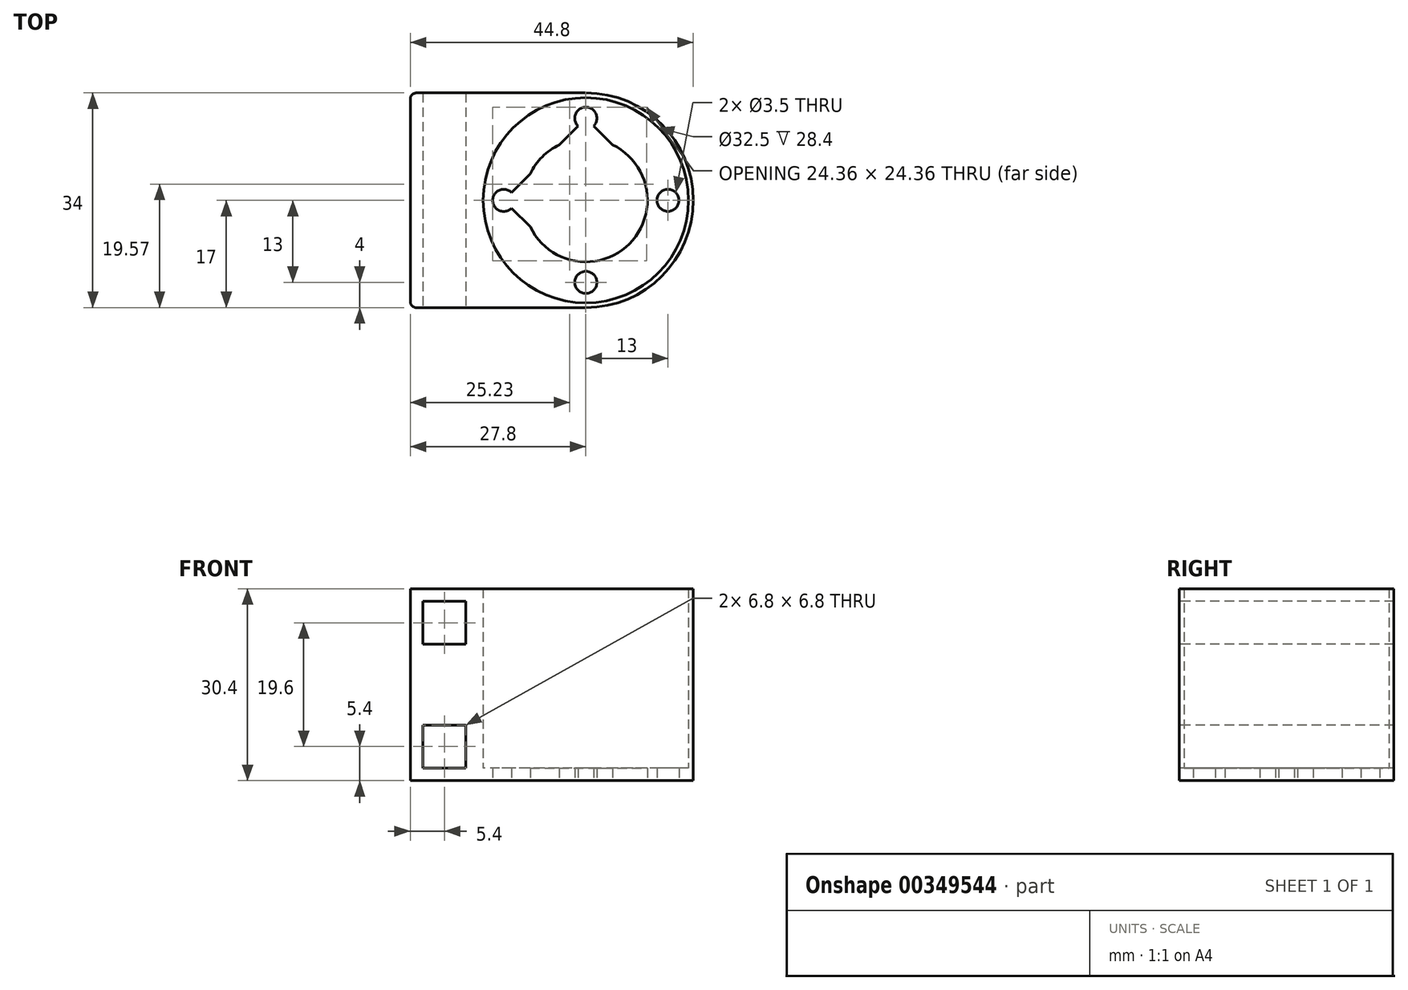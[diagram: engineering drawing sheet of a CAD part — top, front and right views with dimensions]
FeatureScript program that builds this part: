
annotation { "Feature Type Name" : "Feature", "Feature Type Description" : "" }
export const myFeature = defineFeature(function(context is Context, id is Id, definition is map)
    precondition{}
    {
        {
            var Q0;
            Q0=qCreatedBy(makeId("Top.planeOp"),FACE);
            var sketch = newSketch(context, id + "F0", { "sketchPlane" : qUnion([Q0])});
            skCircle(sketch, "E0", {"center": v(0, 0) * mm, "radius": 16.25 * mm});
            skCircle(sketch, "E1", {"center": v(0, 0) * mm, "radius": 17 * mm});
            skLineSegment(sketch, "E2", {"start": v(0, 0) * mm, "end": v(0, 17) * mm});
            skLineSegment(sketch, "E3.bottom", {"start": v(0, 17) * mm, "end": v(-27.8, 17) * mm});
            skLineSegment(sketch, "E3.top", {"start": v(0, -17) * mm, "end": v(-27.8, -17) * mm});
            skLineSegment(sketch, "E3.left", {"start": v(0, 17) * mm, "end": v(0, -17) * mm});
            skLineSegment(sketch, "E3.right", {"start": v(-27.8, 17) * mm, "end": v(-27.8, -17) * mm});
            skCircle(sketch, "E4", {"center": v(0, 0) * mm, "radius": 9.75 * mm});
            skCircle(sketch, "E5.cCircle", {"center": v(0, 0) * mm, "radius": 13 * mm, "construction": true});
            skLineSegment(sketch, "E5.0", {"start": v(0, -13) * mm, "end": v(-13, 0) * mm});
            skLineSegment(sketch, "E5.1", {"start": v(-13, 0) * mm, "end": v(0, 13) * mm});
            skLineSegment(sketch, "E5.2", {"start": v(0, 13) * mm, "end": v(13, 0) * mm});
            skLineSegment(sketch, "E5.3", {"start": v(13, 0) * mm, "end": v(0, -13) * mm});
            skCircle(sketch, "E6", {"center": v(0, 13) * mm, "radius": 1.75 * mm});
            skCircle(sketch, "E7", {"center": v(13, 0) * mm, "radius": 1.75 * mm});
            skCircle(sketch, "E8", {"center": v(0, -13) * mm, "radius": 1.75 * mm});
            skCircle(sketch, "E9", {"center": v(-13, 0) * mm, "radius": 1.75 * mm});
            skSolve(sketch);
        }
        {
            var Q0;
            {var subQ1=sQuery(id+"F0.wireOp",EDGE,"E3.bottom");Q0=makeQuery(id+"F0.imprint","IMPRINT",FACE,{"disambiguationData":[TD([[makeQuery(id+"F0.imprint","IMPRINT",EDGE,{"derivedFrom":subQ1}),1.0]])]});}
            var Q1;
            {var subQ0=sQuery(id+"F0.wireOp",EDGE,"E3.left");var subQ1=sQuery(id+"F0.wireOp",EDGE,"E0");var subQ2=makeQuery(id+"F0.imprint","INTERSECT",VERTEX,{"disambiguationData":[OD(0.0)],"derivedFrom":[subQ1,subQ0]});Q1=makeQuery(id+"F0.imprint","IMPRINT",FACE,{"disambiguationData":[TD([[makeQuery(id+"F0.imprint","IMPRINT",EDGE,{"disambiguationData":[TD([[subQ2,-1.0]])],"derivedFrom":subQ1}),-1.0]])]});}
            var Q2;
            {var subQ0=sQuery(id+"F0.wireOp",EDGE,"E3.left");var subQ1=sQuery(id+"F0.wireOp",EDGE,"E0");var subQ2=makeQuery(id+"F0.imprint","INTERSECT",VERTEX,{"disambiguationData":[OD(0.0)],"derivedFrom":[subQ1,subQ0]});Q2=makeQuery(id+"F0.imprint","IMPRINT",FACE,{"disambiguationData":[TD([[makeQuery(id+"F0.imprint","IMPRINT",EDGE,{"disambiguationData":[TD([[subQ2,1.0]])],"derivedFrom":subQ1}),-1.0]])]});}
            extrude(context, id + "F1", {"entities" : qUnion([Q0, Q1, Q2]), "depth" : 30.4 * mm});
        }
        {
            var Q0;
            {var subQ5=sQuery(id+"F0.wireOp",EDGE,"E3.left");var subQ6=sQuery(id+"F0.wireOp",EDGE,"E0");var subQ7=makeQuery(id+"F0.imprint","INTERSECT",VERTEX,{"disambiguationData":[OD(0.0)],"derivedFrom":[subQ6,subQ5]});Q0=makeQuery(id+"F0.imprint","IMPRINT",FACE,{"disambiguationData":[TD([[makeQuery(id+"F0.imprint","IMPRINT",EDGE,{"disambiguationData":[TD([[subQ7,1.0]])],"derivedFrom":subQ6}),1.0]])]});}
            var Q1;
            {var subQ12=sQuery(id+"F0.wireOp",EDGE,"E3.left");var subQ13=sQuery(id+"F0.wireOp",EDGE,"E0");var subQ14=makeQuery(id+"F0.imprint","INTERSECT",VERTEX,{"disambiguationData":[OD(0.0)],"derivedFrom":[subQ13,subQ12]});Q1=makeQuery(id+"F0.imprint","IMPRINT",FACE,{"disambiguationData":[TD([[makeQuery(id+"F0.imprint","IMPRINT",EDGE,{"disambiguationData":[TD([[subQ14,-1.0]])],"derivedFrom":subQ13}),1.0]])]});}
            var Q2;
            {var subQ0=sQuery(id+"F0.wireOp",EDGE,"E6");var subQ1=sQuery(id+"F0.wireOp",EDGE,"E3.left");var subQ2=makeQuery(id+"F0.imprint","INTERSECT",VERTEX,{"disambiguationData":[OD(1.0)],"derivedFrom":[subQ1,subQ0]});Q2=makeQuery(id+"F0.imprint","IMPRINT",FACE,{"disambiguationData":[TD([[makeQuery(id+"F0.imprint","IMPRINT",EDGE,{"disambiguationData":[TD([[subQ2,-1.0]])],"derivedFrom":subQ1}),-1.0]])]});}
            var Q3;
            {var subQ0=sQuery(id+"F0.wireOp",EDGE,"E6");var subQ1=sQuery(id+"F0.wireOp",EDGE,"E3.left");var subQ2=makeQuery(id+"F0.imprint","INTERSECT",VERTEX,{"disambiguationData":[OD(1.0)],"derivedFrom":[subQ1,subQ0]});Q3=makeQuery(id+"F0.imprint","IMPRINT",FACE,{"disambiguationData":[TD([[makeQuery(id+"F0.imprint","IMPRINT",EDGE,{"disambiguationData":[TD([[subQ2,-1.0]])],"derivedFrom":subQ1}),1.0]])]});}
            var Q4;
            {var subQ0=sQuery(id+"F0.wireOp",EDGE,"E5.1");var subQ1=sQuery(id+"F0.wireOp",EDGE,"E4");var subQ2=makeQuery(id+"F0.imprint","INTERSECT",VERTEX,{"disambiguationData":[OD(1.0)],"derivedFrom":[subQ1,subQ0]});Q4=makeQuery(id+"F0.imprint","IMPRINT",FACE,{"disambiguationData":[TD([[makeQuery(id+"F0.imprint","IMPRINT",EDGE,{"disambiguationData":[TD([[subQ2,-1.0]])],"derivedFrom":subQ1}),-1.0]])]});}
            var Q5;
            {var subQ0=sQuery(id+"F0.wireOp",EDGE,"E5.2");var subQ1=sQuery(id+"F0.wireOp",EDGE,"E4");var subQ2=makeQuery(id+"F0.imprint","INTERSECT",VERTEX,{"disambiguationData":[OD(1.0)],"derivedFrom":[subQ1,subQ0]});Q5=makeQuery(id+"F0.imprint","IMPRINT",FACE,{"disambiguationData":[TD([[makeQuery(id+"F0.imprint","IMPRINT",EDGE,{"disambiguationData":[TD([[subQ2,1.0]])],"derivedFrom":subQ1}),-1.0]])]});}
            var Q6;
            {var subQ0=sQuery(id+"F0.wireOp",EDGE,"E4");var subQ1=sQuery(id+"F0.wireOp",EDGE,"E3.left");var subQ2=makeQuery(id+"F0.imprint","INTERSECT",VERTEX,{"disambiguationData":[OD(1.0)],"derivedFrom":[subQ1,subQ0]});Q6=makeQuery(id+"F0.imprint","IMPRINT",FACE,{"disambiguationData":[TD([[makeQuery(id+"F0.imprint","IMPRINT",EDGE,{"disambiguationData":[TD([[subQ2,-1.0]])],"derivedFrom":subQ1}),1.0]])]});}
            var Q7;
            {var subQ0=sQuery(id+"F0.wireOp",EDGE,"E4");var subQ1=sQuery(id+"F0.wireOp",EDGE,"E3.left");var subQ2=makeQuery(id+"F0.imprint","INTERSECT",VERTEX,{"disambiguationData":[OD(1.0)],"derivedFrom":[subQ1,subQ0]});Q7=makeQuery(id+"F0.imprint","IMPRINT",FACE,{"disambiguationData":[TD([[makeQuery(id+"F0.imprint","IMPRINT",EDGE,{"disambiguationData":[TD([[subQ2,-1.0]])],"derivedFrom":subQ1}),-1.0]])]});}
            extrude(context, id + "F2", {"entities" : qUnion([Q0, Q1, Q2, Q3, Q4, Q5, Q6, Q7]), "operationType" : NewBodyOperationType.ADD, "depth" : 2 * mm});
        }
        {
            var Q0;
            Q0=makeQuery(id+"F1.opExtrude","SWEPT_FACE",FACE,{"disambiguationData":[OSD([sQuery(id+"F0.wireOp",EDGE,"E3.top")])]});
            var sketch = newSketch(context, id + "F3", { "sketchPlane" : qUnion([Q0])});
            skLineSegment(sketch, "E10.bottom", {"start": v(-27.8, 30.4) * mm, "end": v(-25.8, 30.4) * mm});
            skLineSegment(sketch, "E10.top", {"start": v(-27.8, 28.4) * mm, "end": v(-25.8, 28.4) * mm});
            skLineSegment(sketch, "E10.left", {"start": v(-27.8, 30.4) * mm, "end": v(-27.8, 28.4) * mm});
            skLineSegment(sketch, "E10.right", {"start": v(-25.8, 30.4) * mm, "end": v(-25.8, 28.4) * mm});
            skLineSegment(sketch, "E11.bottom", {"start": v(-25.8, 28.4) * mm, "end": v(-19, 28.4) * mm});
            skLineSegment(sketch, "E11.top", {"start": v(-25.8, 21.6) * mm, "end": v(-19, 21.6) * mm});
            skLineSegment(sketch, "E11.left", {"start": v(-25.8, 28.4) * mm, "end": v(-25.8, 21.6) * mm});
            skLineSegment(sketch, "E11.right", {"start": v(-19, 28.4) * mm, "end": v(-19, 21.6) * mm});
            skPoint(sketch, "E12", {"position": v(-27.8, 15.2) * mm});
            skLineSegment(sketch, "E13", {"start": v(-27.8, 15.2) * mm, "end": v(0, 15.2) * mm});
            skLineSegment(sketch, "E14.MirrorCS", {"start": v(-25.8, 8.8) * mm, "end": v(-19, 8.8) * mm});
            skLineSegment(sketch, "E15.MirrorCS", {"start": v(-19, 2) * mm, "end": v(-19, 8.8) * mm});
            skLineSegment(sketch, "E16.MirrorCS", {"start": v(-25.8, 2) * mm, "end": v(-19, 2) * mm});
            skLineSegment(sketch, "E17.MirrorCS", {"start": v(-25.8, 2) * mm, "end": v(-25.8, 8.8) * mm});
            skSolve(sketch);
        }
        {
            var Q0;
            Q0=makeQuery(id+"F3.imprint","IMPRINT",FACE,{"disambiguationData":[TD([[makeQuery(id+"F3.imprint","IMPRINT",EDGE,{"derivedFrom":sQuery(id+"F3.wireOp",EDGE,"E11.bottom")}),-1.0]])]});
            var Q1;
            Q1=makeQuery(id+"F3.imprint","IMPRINT",FACE,{"disambiguationData":[TD([[makeQuery(id+"F3.imprint","IMPRINT",EDGE,{"derivedFrom":sQuery(id+"F3.wireOp",EDGE,"E14.MirrorCS")}),-1.0]])]});
            extrude(context, id + "F4", {"entities" : qUnion([Q0, Q1]), "operationType" : NewBodyOperationType.REMOVE, "oppositeDirection" : true, "depth" : 50 * mm});
        }
        {
            var Q0;
            Q0=makeQuery(id+"F1.opExtrude","SWEPT_EDGE",EDGE,{"disambiguationData":[OSD([sQuery(id+"F0.wireOp",EDGE,"E3.bottom"),sQuery(id+"F0.wireOp",EDGE,"E3.right")])]});
            var Q1;
            Q1=makeQuery(id+"F1.opExtrude","SWEPT_EDGE",EDGE,{"disambiguationData":[OSD([sQuery(id+"F0.wireOp",EDGE,"E3.top"),sQuery(id+"F0.wireOp",EDGE,"E3.right")])]});
            fillet(context, id + "F5", {"entities" : qUnion([Q0, Q1]), "radius" : 1 * mm, "tangentPropagation" : true, "allowEdgeOverflow" : false});
        }
    });
